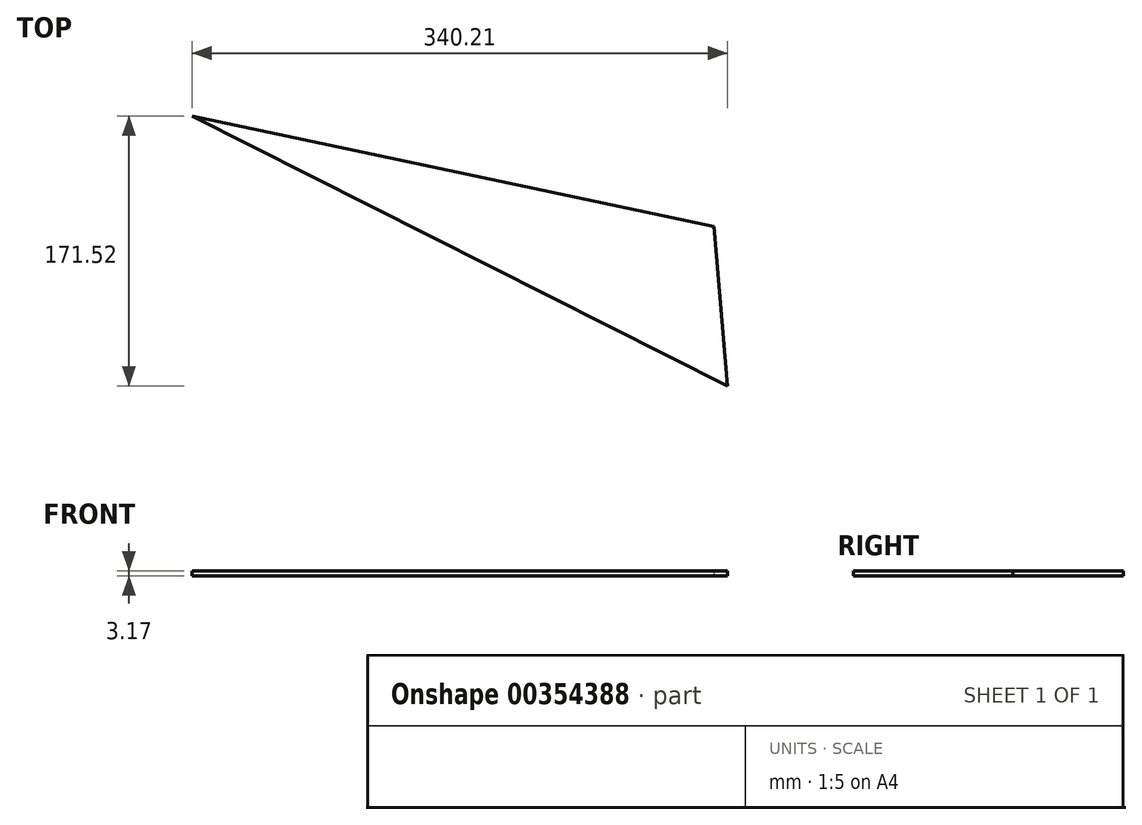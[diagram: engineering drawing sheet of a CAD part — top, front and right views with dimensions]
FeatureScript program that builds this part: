
annotation { "Feature Type Name" : "Feature", "Feature Type Description" : "" }
export const myFeature = defineFeature(function(context is Context, id is Id, definition is map)
    precondition{}
    {
        {
            var Q0;
            Q0=qCreatedBy(makeId("Top.planeOp"),FACE);
            var sketch = newSketch(context, id + "F0", { "sketchPlane" : qUnion([Q0])});
            skLineSegment(sketch, "E0", {"start": v(121.07, -84.13) * mm, "end": v(112.31, 17.09) * mm});
            skLineSegment(sketch, "E1", {"start": v(112.31, 17.09) * mm, "end": v(-219.14, 87.39) * mm});
            skLineSegment(sketch, "E2", {"start": v(-219.14, 87.39) * mm, "end": v(121.07, -84.13) * mm});
            skSolve(sketch);
        }
        {
            var Q0;
            Q0 = qSketchRegion(id + "F0", true);
            extrude(context, id + "F1", {"entities" : qUnion([Q0]), "depth" : 3.17 * mm});
        }
    });
